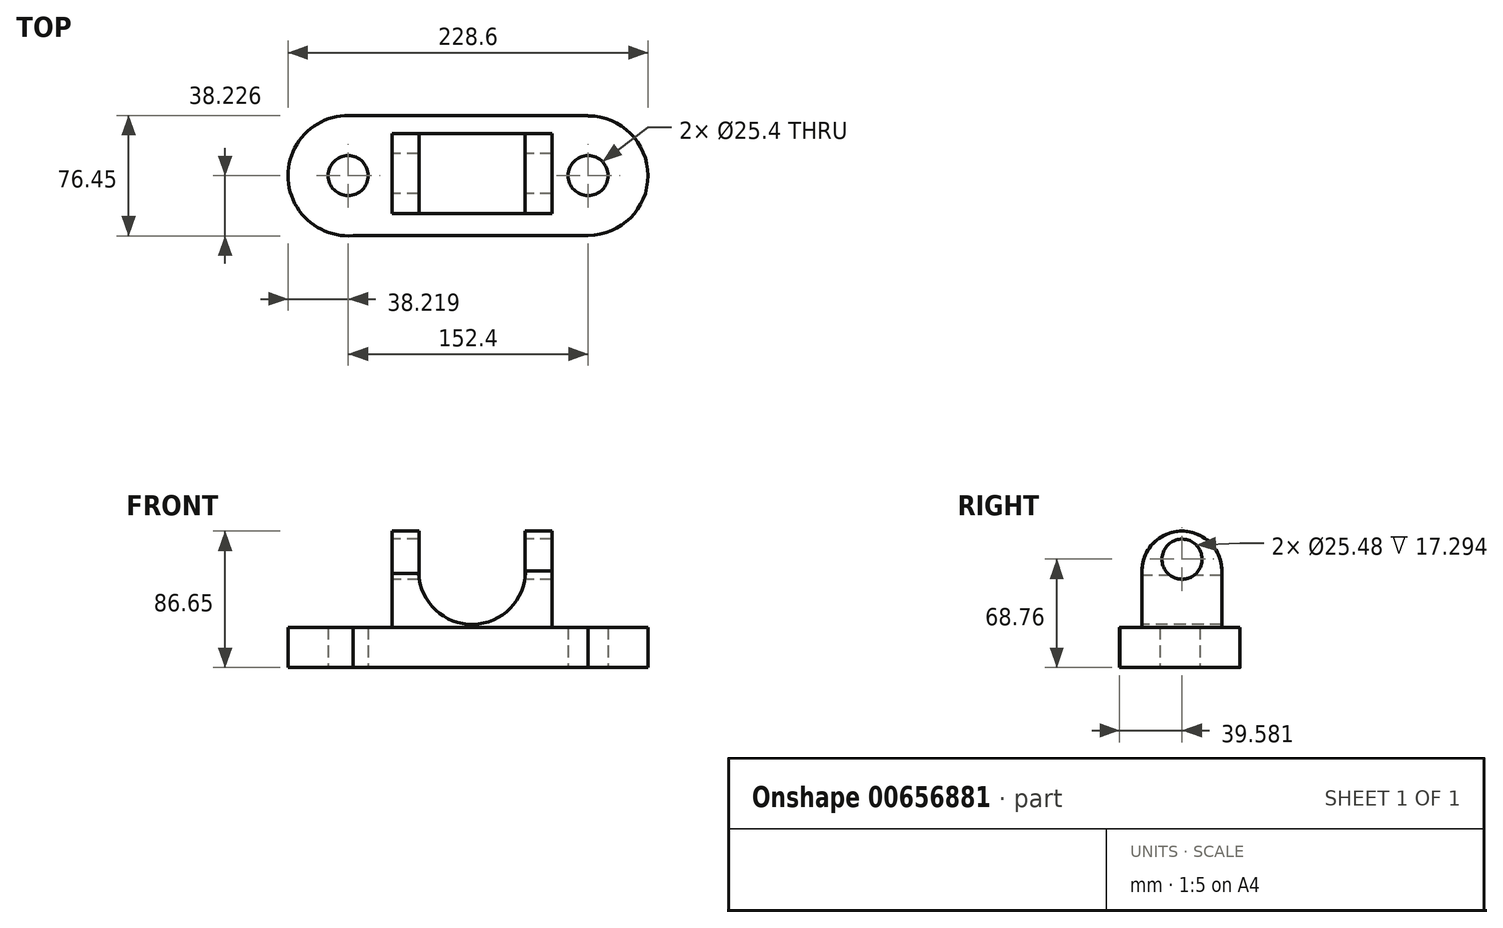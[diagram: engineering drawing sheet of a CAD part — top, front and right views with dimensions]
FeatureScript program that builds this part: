
annotation { "Feature Type Name" : "Feature", "Feature Type Description" : "" }
export const myFeature = defineFeature(function(context is Context, id is Id, definition is map)
    precondition{}
    {
        {
            var Q0;
            Q0=qCreatedBy(makeId("Top.planeOp"),FACE);
            var sketch = newSketch(context, id + "F0", { "sketchPlane" : qUnion([Q0])});
            skLineSegment(sketch, "E0.bottom", {"start": v(-87.23, 28.18) * mm, "end": v(65.17, 28.18) * mm});
            skLineSegment(sketch, "E0.top", {"start": v(-87.23, -48.02) * mm, "end": v(65.17, -48.02) * mm});
            skLineSegment(sketch, "E0.right", {"start": v(65.17, 28.18) * mm, "end": v(65.17, 28.06) * mm});
            skArc(sketch, "E1", {"start": v(-84.17, 28.18) * mm, "mid": v(-125.45, -9.92) * mm, "end": v(-84.17, -48.02) * mm});
            skArc(sketch, "E2", {"start": v(65.17, -47.9) * mm, "mid": v(103.15, -9.92) * mm, "end": v(65.17, 28.06) * mm});
            skLineSegment(sketch, "E3.trimOffspring", {"start": v(65.17, -47.9) * mm, "end": v(65.17, -48.02) * mm});
            skCircle(sketch, "E4", {"center": v(-87.23, -9.92) * mm, "radius": 12.7 * mm});
            skCircle(sketch, "E5", {"center": v(65.17, -9.92) * mm, "radius": 12.7 * mm});
            skSolve(sketch);
        }
        {
            var Q0;
            {var subQ1=sQuery(id+"F0.wireOp",EDGE,"E0.right");Q0=makeQuery(id+"F0.imprint","IMPRINT",FACE,{"disambiguationData":[TD([[makeQuery(id+"F0.imprint","IMPRINT",EDGE,{"derivedFrom":subQ1}),-1.0]])]});}
            extrude(context, id + "F1", {"entities" : qUnion([Q0]), "depth" : 25.4 * mm, "offsetDistance" : 25.4 * mm});
        }
        {
            var Q0;
            Q0=makeQuery(id+"F1.opExtrude","CAP_FACE",FACE,{"disambiguationData":[OSD([sQuery(id+"F0.wireOp",EDGE,"E0.bottom"),sQuery(id+"F0.wireOp",EDGE,"E0.top"),sQuery(id+"F0.wireOp",EDGE,"E0.right"),sQuery(id+"F0.wireOp",EDGE,"E1"),sQuery(id+"F0.wireOp",EDGE,"E2"),sQuery(id+"F0.wireOp",EDGE,"E3.trimOffspring"),sQuery(id+"F0.wireOp",EDGE,"E4"),sQuery(id+"F0.wireOp",EDGE,"E5")])],"isStart":false});
            var sketch = newSketch(context, id + "F2", { "sketchPlane" : qUnion([Q0])});
            skLineSegment(sketch, "E6.bottom", {"start": v(-59.38, 16.79) * mm, "end": v(42.22, 16.79) * mm});
            skLineSegment(sketch, "E6.top", {"start": v(-59.38, -34.01) * mm, "end": v(42.22, -34.01) * mm});
            skLineSegment(sketch, "E6.left", {"start": v(-59.38, 16.79) * mm, "end": v(-59.38, -34.01) * mm});
            skLineSegment(sketch, "E6.right", {"start": v(42.22, 16.79) * mm, "end": v(42.22, -34.01) * mm});
            skSolve(sketch);
        }
        {
            var Q0;
            Q0=qSketchRegion(id+"F2",true);
            extrude(context, id + "F3", {"entities" : qUnion([Q0]), "operationType" : NewBodyOperationType.ADD, "depth" : 35.81 * mm, "offsetDistance" : 25.4 * mm});
        }
        {
            var Q0;
            Q0=makeQuery(id+"F3.opExtrude","SWEPT_FACE",FACE,{"disambiguationData":[OSD([sQuery(id+"F2.wireOp",EDGE,"E6.top")])]});
            var sketch = newSketch(context, id + "F4", { "sketchPlane" : qUnion([Q0])});
            skCircle(sketch, "E7", {"center": v(-8.58, 61.21) * mm, "radius": 33.9 * mm});
            skSolve(sketch);
        }
        {
            var Q0;
            Q0=qSketchRegion(id+"F4",true);
            extrude(context, id + "F5", {"entities" : qUnion([Q0]), "operationType" : NewBodyOperationType.REMOVE, "oppositeDirection" : true, "depth" : 57.66 * mm, "offsetDistance" : 25.4 * mm});
        }
        {
            var Q0;
            Q0=makeQuery(id+"F3.opExtrude","SWEPT_FACE",FACE,{"disambiguationData":[OSD([sQuery(id+"F2.wireOp",EDGE,"E6.left")])]});
            var sketch = newSketch(context, id + "F6", { "sketchPlane" : qUnion([Q0])});
            skCircle(sketch, "E8", {"center": v(8.61, 61.21) * mm, "radius": 25.44 * mm});
            skSolve(sketch);
        }
        {
            var Q0;
            Q0=qSketchRegion(id+"F6",true);
            extrude(context, id + "F7", {"entities" : qUnion([Q0]), "operationType" : NewBodyOperationType.ADD, "oppositeDirection" : true, "depth" : 17.02 * mm, "offsetDistance" : 25.4 * mm});
        }
        {
            var Q0;
            Q0=makeQuery(id+"F3.opExtrude","SWEPT_FACE",FACE,{"disambiguationData":[OSD([sQuery(id+"F2.wireOp",EDGE,"E6.right")])]});
            var sketch = newSketch(context, id + "F8", { "sketchPlane" : qUnion([Q0])});
            skCircle(sketch, "E9", {"center": v(-8.61, 61.21) * mm, "radius": 25.36 * mm});
            skSolve(sketch);
        }
        {
            var Q0;
            Q0=qSketchRegion(id+"F8",true);
            extrude(context, id + "F9", {"entities" : qUnion([Q0]), "operationType" : NewBodyOperationType.ADD, "oppositeDirection" : true, "depth" : 17.02 * mm, "offsetDistance" : 25.4 * mm});
        }
        {
            var Q0;
            Q0=makeQuery(id+"F7.boolean.opBoolean","MERGE",FACE,{"derivedFrom":[makeQuery(id+"F3.opExtrude","SWEPT_FACE",FACE,{"disambiguationData":[OSD([sQuery(id+"F2.wireOp",EDGE,"E6.left")])]}),makeQuery(id+"F7.opExtrude","CAP_FACE",FACE,{"disambiguationData":[OSD([sQuery(id+"F6.wireOp",EDGE,"E8")])],"isStart":true})]});
            var sketch = newSketch(context, id + "F10", { "sketchPlane" : qUnion([Q0])});
            skCircle(sketch, "E10", {"center": v(8.57, 68.76) * mm, "radius": 12.74 * mm});
            skSolve(sketch);
        }
        {
            var Q0;
            Q0=qSketchRegion(id+"F10",true);
            extrude(context, id + "F11", {"entities" : qUnion([Q0]), "operationType" : NewBodyOperationType.REMOVE, "oppositeDirection" : true, "depth" : 121.67 * mm, "offsetDistance" : 25.4 * mm});
        }
    });
